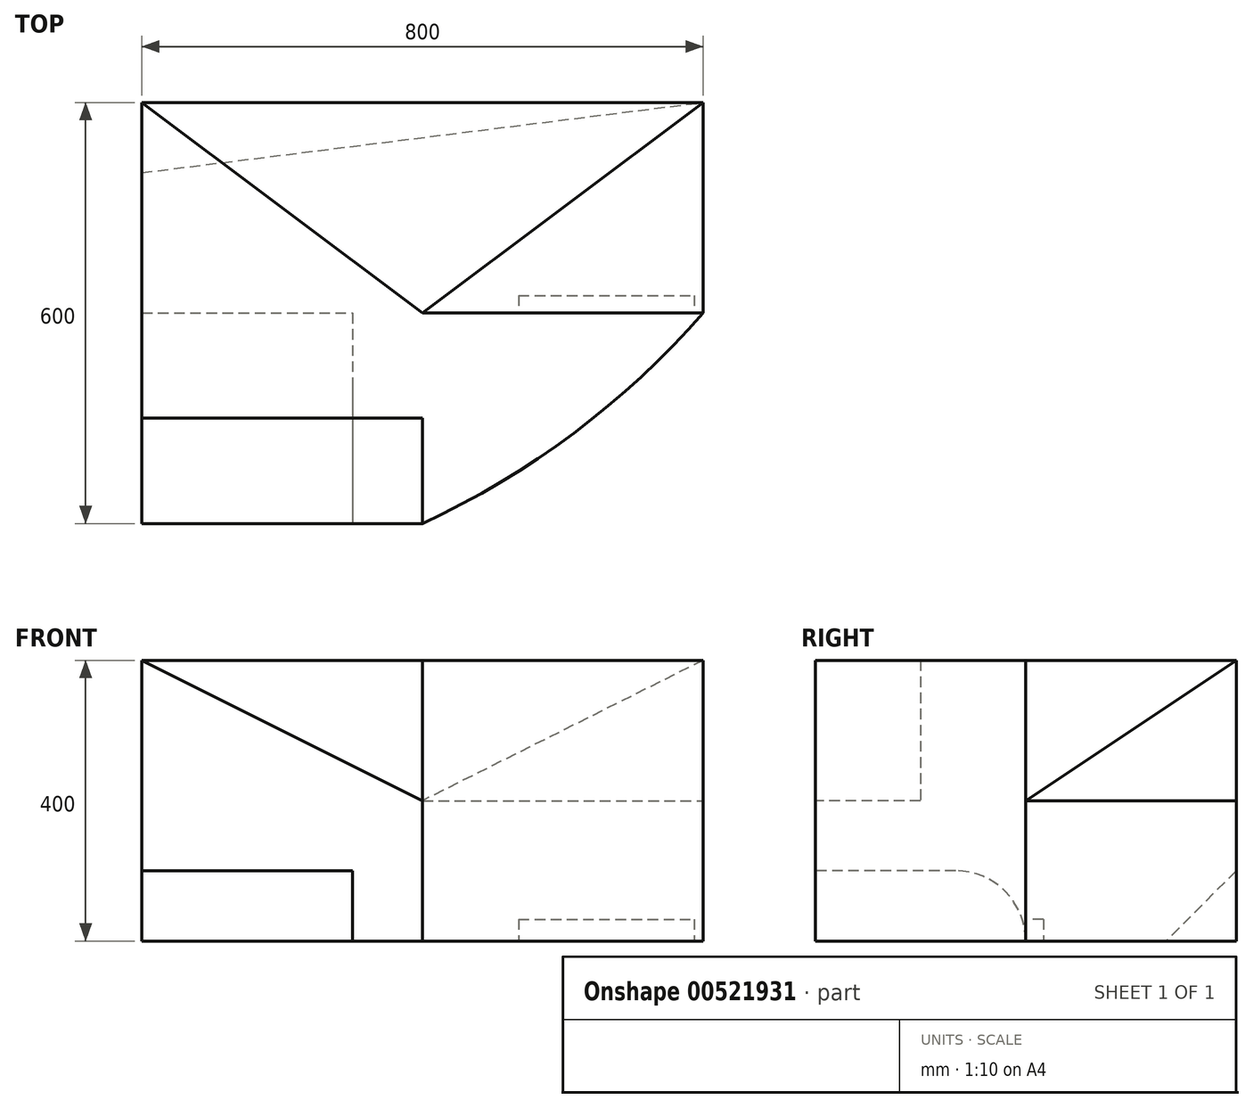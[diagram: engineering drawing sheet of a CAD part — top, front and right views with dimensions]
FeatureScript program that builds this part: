
annotation { "Feature Type Name" : "Feature", "Feature Type Description" : "" }
export const myFeature = defineFeature(function(context is Context, id is Id, definition is map)
    precondition{}
    {
        {
            var Q0;
            Q0=qCreatedBy(makeId("Top.planeOp"),FACE);
            var sketch = newSketch(context, id + "F0", { "sketchPlane" : qUnion([Q0])});
            skLineSegment(sketch, "E0.bottom", {"start": v(-400, 300) * mm, "end": v(400, 300) * mm});
            skLineSegment(sketch, "E0.top", {"start": v(-400, -300) * mm, "end": v(400, -300) * mm});
            skLineSegment(sketch, "E0.left", {"start": v(-400, 300) * mm, "end": v(-400, -300) * mm});
            skLineSegment(sketch, "E0.right", {"start": v(400, 300) * mm, "end": v(400, -300) * mm});
            skSolve(sketch);
        }
        {
            var Q0;
            Q0 = qSketchRegion(id + "F0", true);
            extrude(context, id + "F1", {"entities" : qUnion([Q0]), "depth" : 400 * mm, "offsetDistance" : 25 * mm});
        }
        {
            var Q0;
            Q0=makeQuery(id+"F1.opExtrude","CAP_FACE",FACE,{"disambiguationData":[OSD([sQuery(id+"F0.wireOp",EDGE,"E0.bottom"),sQuery(id+"F0.wireOp",EDGE,"E0.top"),sQuery(id+"F0.wireOp",EDGE,"E0.left"),sQuery(id+"F0.wireOp",EDGE,"E0.right")])],"isStart":false});
            var sketch = newSketch(context, id + "F2", { "sketchPlane" : qUnion([Q0])});
            skLineSegment(sketch, "E1", {"start": v(-400, 300) * mm, "end": v(0, 0) * mm});
            skLineSegment(sketch, "E2", {"start": v(0, 0) * mm, "end": v(400, 0) * mm});
            skLineSegment(sketch, "E3", {"start": v(-400, -150) * mm, "end": v(0, -150) * mm});
            skLineSegment(sketch, "E4", {"start": v(0, -150) * mm, "end": v(0, -300) * mm});
            skArc(sketch, "E5", {"start": v(0, -300) * mm, "mid": v(215.8, -171.06) * mm, "end": v(400, 0) * mm});
            skSolve(sketch);
        }
        {
            var Q0;
            {var subQ0=sQuery(id+"F2.wireOp",EDGE,"E5");Q0=makeQuery(id+"F2.imprint","IMPRINT",FACE,{"disambiguationData":[TD([[makeQuery(id+"F2.imprint","IMPRINT",EDGE,{"derivedFrom":subQ0}),-1.0]])]});}
            extrude(context, id + "F3", {"entities" : qUnion([Q0]), "operationType" : NewBodyOperationType.REMOVE, "endBound" : BoundingType.UP_TO_NEXT, "oppositeDirection" : true, "depth" : 25 * mm, "offsetDistance" : 25 * mm});
        }
        {
            var Q0;
            Q0=makeQuery(id+"F1.opExtrude","SWEPT_FACE",FACE,{"disambiguationData":[OSD([sQuery(id+"F0.wireOp",EDGE,"E0.top")])]});
            var sketch = newSketch(context, id + "F4", { "sketchPlane" : qUnion([Q0])});
            skLineSegment(sketch, "E6", {"start": v(-400, 400) * mm, "end": v(0, 200) * mm});
            skLineSegment(sketch, "E7", {"start": v(0, 200) * mm, "end": v(0, 400) * mm});
            skLineSegment(sketch, "E8", {"start": v(0, 400) * mm, "end": v(-400, 400) * mm});
            skSolve(sketch);
        }
        {
            var Q0;
            Q0=makeQuery(id+"F4.imprint","IMPRINT",FACE,{"disambiguationData":[TD([[makeQuery(id+"F4.imprint","IMPRINT",EDGE,{"derivedFrom":sQuery(id+"F4.wireOp",EDGE,"E6")}),1.0]])]});
            extrude(context, id + "F5", {"entities" : qUnion([Q0]), "operationType" : NewBodyOperationType.REMOVE, "oppositeDirection" : true, "depth" : 150 * mm, "offsetDistance" : 25 * mm});
        }
        {
            var Q0;
            Q0=qCreatedBy(makeId("Right.planeOp"),FACE);
            var sketch = newSketch(context, id + "F6", { "sketchPlane" : qUnion([Q0])});
            skLineSegment(sketch, "E9", {"start": v(0, 0) * mm, "end": v(0, 200) * mm});
            skSolve(sketch);
        }
        {
            var Q0;
            Q0=sQuery(id+"F6.wireOp",VERTEX,"E9.end");
            var Q1;
            Q1=sQuery(id+"F2.wireOp",VERTEX,"E1.start");
            var Q2;
            Q2=makeQuery(id+"F1.opExtrude","CAP_VERTEX",VERTEX,{"disambiguationData":[OSD([sQuery(id+"F0.wireOp",EDGE,"E0.bottom"),sQuery(id+"F0.wireOp",EDGE,"E0.right")])],"isStart":false});
            cPlane(context, id + "F7", {"entities" : qUnion([Q0, Q1, Q2]), "cplaneType" : CPlaneType.THREE_POINT, "offset" : 25 * mm, "width" : 150 * mm, "height" : 150 * mm});
        }
        {
            var Q0;
            Q0=makeQuery(id+"F2.imprint","IMPRINT",FACE,{"disambiguationData":[TD([[makeQuery(id+"F2.imprint","IMPRINT",EDGE,{"derivedFrom":sQuery(id+"F2.wireOp",EDGE,"E1")}),1.0]])]});
            var sketch = newSketch(context, id + "F8", { "sketchPlane" : qUnion([Q0])});
            skLineSegment(sketch, "E10", {"start": v(0, 0) * mm, "end": v(400, 300) * mm});
            skLineSegment(sketch, "E11.0", {"start": v(-400, 300) * mm, "end": v(0, 0) * mm});
            skLineSegment(sketch, "E12.0", {"start": v(-400, 300) * mm, "end": v(400, 300) * mm});
            skSolve(sketch);
        }
        {
            var Q0;
            Q0 = qSketchRegion(id + "F8", true);
            var Q1;
            Q1=qCreatedBy(id+"F7.planeOp",FACE);
            extrude(context, id + "F9", {"entities" : qUnion([Q0]), "operationType" : NewBodyOperationType.REMOVE, "endBound" : BoundingType.UP_TO_SURFACE, "oppositeDirection" : true, "depth" : 25 * mm, "endBoundEntityFace" : qUnion([Q1]), "offsetDistance" : 25 * mm});
        }
        {
            var Q0;
            Q0=makeQuery(id+"F0.imprint","IMPRINT",FACE,{"disambiguationData":[TD([[makeQuery(id+"F0.imprint","IMPRINT",EDGE,{"derivedFrom":sQuery(id+"F0.wireOp",EDGE,"E0.bottom")}),-1.0]])]});
            cPlane(context, id + "F10", {"entities" : qUnion([Q0]), "cplaneType" : CPlaneType.OFFSET, "offset" : 200 * mm, "width" : 150 * mm, "height" : 150 * mm});
        }
        {
            var Q0;
            Q0=qCreatedBy(id+"F10.planeOp",FACE);
            var sketch = newSketch(context, id + "F11", { "sketchPlane" : qUnion([Q0])});
            skLineSegment(sketch, "E13", {"start": v(0, 0) * mm, "end": v(400, 300) * mm});
            skLineSegment(sketch, "E14", {"start": v(400, 300) * mm, "end": v(400, 0) * mm});
            skLineSegment(sketch, "E15", {"start": v(400, 0) * mm, "end": v(0, 0) * mm});
            skSolve(sketch);
        }
        {
            var Q0;
            Q0 = qSketchRegion(id + "F11", true);
            extrude(context, id + "F12", {"entities" : qUnion([Q0]), "operationType" : NewBodyOperationType.REMOVE, "depth" : 200 * mm, "offsetDistance" : 25 * mm});
        }
        {
            var Q0;
            Q0=makeQuery(id+"F1.opExtrude","SWEPT_FACE",FACE,{"disambiguationData":[OSD([sQuery(id+"F0.wireOp",EDGE,"E0.top")])]});
            var sketch = newSketch(context, id + "F13", { "sketchPlane" : qUnion([Q0])});
            skLineSegment(sketch, "E16.bottom", {"start": v(-400, 0) * mm, "end": v(-100, 0) * mm});
            skLineSegment(sketch, "E16.top", {"start": v(-400, 100) * mm, "end": v(-100, 100) * mm});
            skLineSegment(sketch, "E16.left", {"start": v(-400, 0) * mm, "end": v(-400, 100) * mm});
            skLineSegment(sketch, "E16.right", {"start": v(-100, 0) * mm, "end": v(-100, 100) * mm});
            skSolve(sketch);
        }
        {
            var Q0;
            Q0=makeQuery(id+"F13.imprint","IMPRINT",FACE,{"disambiguationData":[TD([[makeQuery(id+"F13.imprint","IMPRINT",EDGE,{"derivedFrom":sQuery(id+"F13.wireOp",EDGE,"E16.bottom")}),1.0]])]});
            extrude(context, id + "F14", {"entities" : qUnion([Q0]), "operationType" : NewBodyOperationType.REMOVE, "oppositeDirection" : true, "depth" : 300 * mm, "offsetDistance" : 25 * mm});
        }
        {
            var Q0;
            Q0=makeQuery(id+"F14.boolean.opBoolean","COPY",EDGE,{"derivedFrom":makeQuery(id+"F14.opExtrude","CAP_EDGE",EDGE,{"disambiguationData":[OSD([sQuery(id+"F13.wireOp",EDGE,"E16.top")])],"isStart":false})});
            fillet(context, id + "F15", {"entities" : qUnion([Q0]), "radius" : 100 * mm, "tangentPropagation" : true, "allowEdgeOverflow" : false});
        }
        {
            var Q0;
            Q0=makeQuery(id+"F1.opExtrude","SWEPT_FACE",FACE,{"disambiguationData":[OSD([sQuery(id+"F0.wireOp",EDGE,"E0.bottom")])]});
            var sketch = newSketch(context, id + "F16", { "sketchPlane" : qUnion([Q0])});
            skLineSegment(sketch, "E17", {"start": v(400, 100) * mm, "end": v(-400, 0) * mm});
            skSolve(sketch);
        }
        {
            var Q0;
            Q0=makeQuery(id+"F1.opExtrude","CAP_FACE",FACE,{"disambiguationData":[OSD([sQuery(id+"F0.wireOp",EDGE,"E0.bottom"),sQuery(id+"F0.wireOp",EDGE,"E0.top"),sQuery(id+"F0.wireOp",EDGE,"E0.left"),sQuery(id+"F0.wireOp",EDGE,"E0.right")])],"isStart":true});
            var sketch = newSketch(context, id + "F17", { "sketchPlane" : qUnion([Q0])});
            skLineSegment(sketch, "E18", {"start": v(-400, -200) * mm, "end": v(400, -300) * mm});
            skSolve(sketch);
        }
        {
            var Q0;
            Q0=sQuery(id+"F16.wireOp",VERTEX,"E17.start");
            var Q1;
            Q1=sQuery(id+"F17.wireOp",VERTEX,"E18.end");
            var Q2;
            Q2=sQuery(id+"F17.wireOp",VERTEX,"E18.start");
            cPlane(context, id + "F18", {"entities" : qUnion([Q0, Q1, Q2]), "cplaneType" : CPlaneType.THREE_POINT, "offset" : 25 * mm, "width" : 150 * mm, "height" : 150 * mm});
        }
        {
            var Q0;
            Q0=qCreatedBy(id+"F18.planeOp",FACE);
            var sketch = newSketch(context, id + "F19", { "sketchPlane" : qUnion([Q0])});
            skLineSegment(sketch, "E19.0", {"start": v(-386, 282.84) * mm, "end": v(417.12, 212.13) * mm});
            skLineSegment(sketch, "E20.0", {"start": v(-386, 141.42) * mm, "end": v(417.12, 212.13) * mm});
            skLineSegment(sketch, "E21", {"start": v(-386, 282.84) * mm, "end": v(-386, 141.42) * mm});
            skSolve(sketch);
        }
        {
            var Q0;
            Q0 = qSketchRegion(id + "F19", true);
            extrude(context, id + "F20", {"entities" : qUnion([Q0]), "operationType" : NewBodyOperationType.REMOVE, "endBound" : BoundingType.UP_TO_NEXT, "oppositeDirection" : true, "depth" : 25 * mm, "offsetDistance" : 25 * mm});
        }
        {
            var Q0;
            Q0=qCreatedBy(makeId("Front.planeOp"),FACE);
            var sketch = newSketch(context, id + "F21", { "sketchPlane" : qUnion([Q0])});
            skLineSegment(sketch, "E22.bottom", {"start": v(136.97, 30.97) * mm, "end": v(387.26, 30.97) * mm});
            skLineSegment(sketch, "E22.top", {"start": v(136.97, -138.35) * mm, "end": v(387.26, -138.35) * mm});
            skLineSegment(sketch, "E22.left", {"start": v(136.97, 30.97) * mm, "end": v(136.97, -138.35) * mm});
            skLineSegment(sketch, "E22.right", {"start": v(387.26, 30.97) * mm, "end": v(387.26, -138.35) * mm});
            skSolve(sketch);
        }
        {
            var Q0;
            Q0=makeQuery(id+"F21.imprint","IMPRINT",FACE,{"disambiguationData":[TD([[makeQuery(id+"F21.imprint","IMPRINT",EDGE,{"derivedFrom":sQuery(id+"F21.wireOp",EDGE,"E22.bottom")}),-1.0]])]});
            extrude(context, id + "F22", {"entities" : qUnion([Q0]), "operationType" : NewBodyOperationType.REMOVE, "oppositeDirection" : true, "depth" : 25 * mm, "offsetDistance" : 25 * mm});
        }
    });
